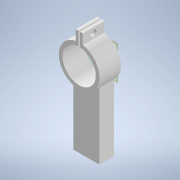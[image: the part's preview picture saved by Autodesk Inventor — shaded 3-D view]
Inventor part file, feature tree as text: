
AUTODESK INVENTOR PART (.ipt)
format: ipt  version: 2022 (Build 260153000, 153)  size: 162,304 bytes
history: native  units: mm
features: extrude x4, sketch x4, reference x4, other x3, plane x2, projected_geometry x1
ambient origin geometry x8: Origin, YZ Plane, XZ Plane, XY Plane, X Axis, Y Axis, Z Axis, Center Point
bodies: Body1 (feature_tree)
feature tree (18):
  plane  "Work Plane3"
  extrude  "Extrusion2"  Depth=1.0mm
  extrude  "Extrusion3"  Depth=2.0mm
  extrude  "Extrusion4"  Depth=14.0mm
  plane  "Work Plane5"
  extrude  "Extrusion5"  Depth=3.0mm
  sketch  "Sketch3"  dims[d8=1.0mm d9=2.5mm]
  reference  "Reference3"
  sketch  "Sketch4"  dims[d10=2.5mm d11=2.0mm]
  projected_geometry  "Projected Loop1"
  sketch  "Sketch5"  dims[d12=7.0mm d13=14.0mm]
  reference  "Reference4"
  sketch  "Sketch7"  dims[d14=15.0mm d15=0.0mm d16=4.03mm d17=15.0mm d18=0.0mm d19=9.0mm d20=15.0mm d21=0.0mm d23=48.0mm d24=15.0mm d25=9.0mm d26=3.0mm d27=0.0mm]
  reference  "Reference5"
  reference  "Reference6"
  other  "Assembly_Final.iam"
  other  "motor:1"
  other  "Base_proyecto:1"
